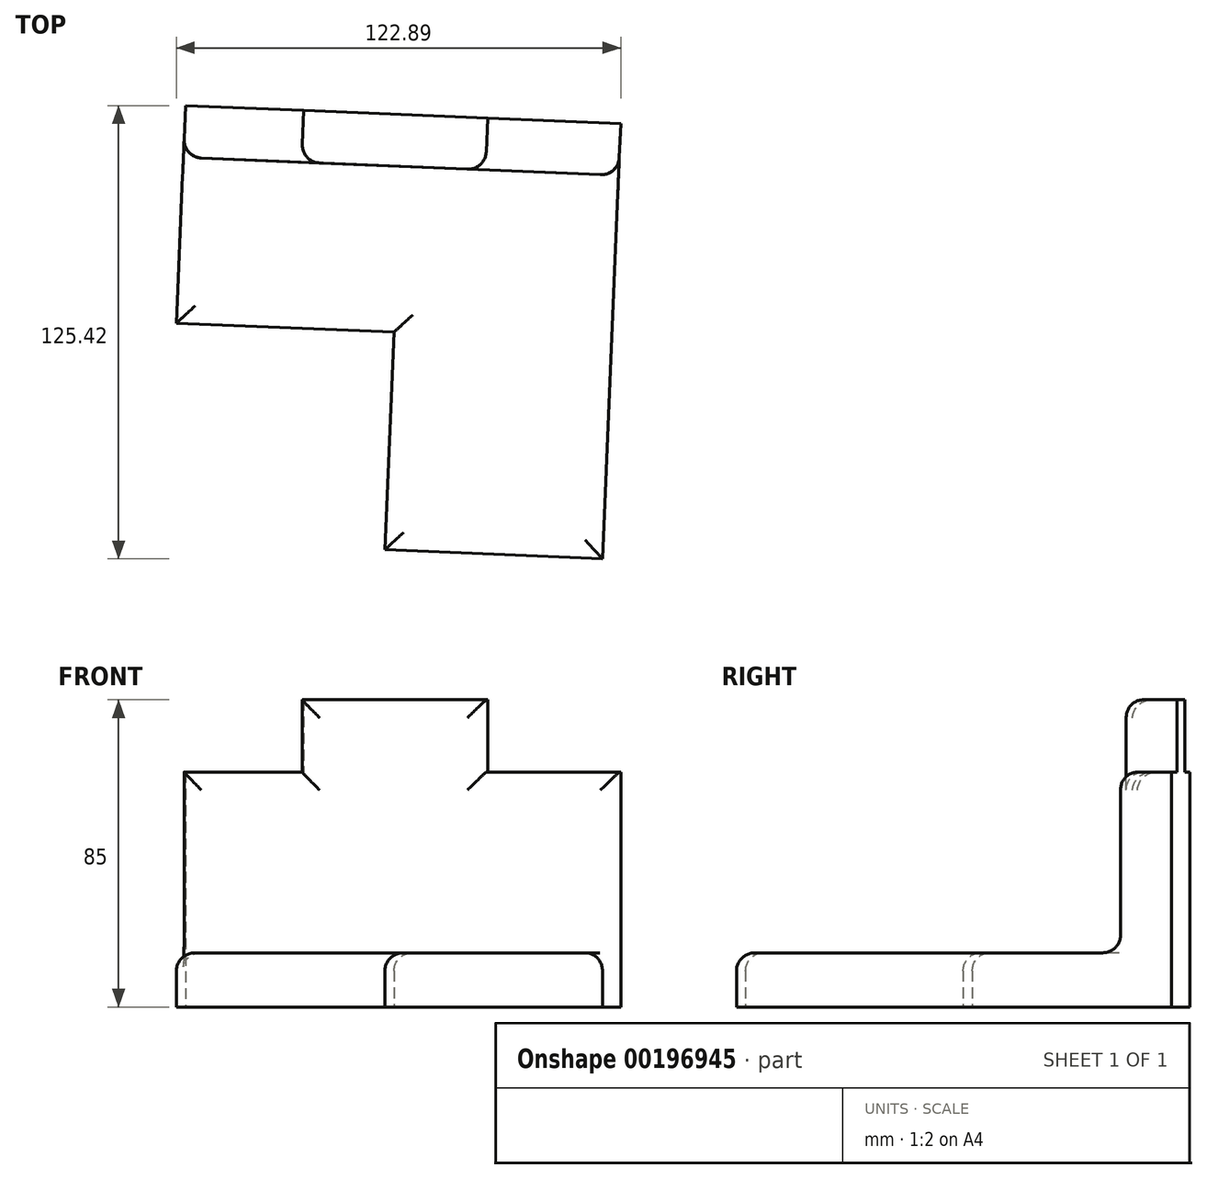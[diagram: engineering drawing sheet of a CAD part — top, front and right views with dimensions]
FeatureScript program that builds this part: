
annotation { "Feature Type Name" : "Feature", "Feature Type Description" : "" }
export const myFeature = defineFeature(function(context is Context, id is Id, definition is map)
    precondition{}
    {
        {
            var Q0;
            Q0=qCreatedBy(makeId("Top.planeOp"),FACE);
            var sketch = newSketch(context, id + "F0", { "sketchPlane" : qUnion([Q0])});
            skLineSegment(sketch, "E0.bottom", {"start": v(-60.23, 60.23) * mm, "end": v(60.23, 60.23) * mm});
            skLineSegment(sketch, "E0.top", {"start": v(0, -60.23) * mm, "end": v(60.23, -60.23) * mm});
            skLineSegment(sketch, "E0.left", {"start": v(-60.23, 60.23) * mm, "end": v(-60.23, 0) * mm});
            skLineSegment(sketch, "E0.right", {"start": v(60.23, 60.23) * mm, "end": v(60.23, -60.23) * mm});
            skPoint(sketch, "E0.middle", {"position": v(0, 0) * mm});
            skLineSegment(sketch, "E1.top", {"start": v(-60.23, 0) * mm, "end": v(0, 0) * mm});
            skLineSegment(sketch, "E1.right", {"start": v(0, -60.23) * mm, "end": v(0, 0) * mm});
            skPoint(sketch, "E2.orphan", {"position": v(-60.23, -60.23) * mm});
            skLineSegment(sketch, "E3", {"start": v(-60.23, 45.92) * mm, "end": v(60.23, 45.92) * mm});
            skSolve(sketch);
        }
        {
            var Q0;
            {var subQ2=sQuery(id+"F0.wireOp",EDGE,"E0.top");Q0=makeQuery(id+"F0.imprint","IMPRINT",FACE,{"disambiguationData":[TD([[makeQuery(id+"F0.imprint","IMPRINT",EDGE,{"derivedFrom":subQ2}),1.0]])]});}
            extrude(context, id + "F1", {"entities" : qUnion([Q0]), "depth" : 15 * mm});
        }
        {
            var Q0;
            {var subQ0=sQuery(id+"F0.wireOp",EDGE,"E0.bottom");Q0=makeQuery(id+"F0.imprint","IMPRINT",FACE,{"disambiguationData":[TD([[makeQuery(id+"F0.imprint","IMPRINT",EDGE,{"derivedFrom":subQ0}),-1.0]])]});}
            extrude(context, id + "F2", {"entities" : qUnion([Q0]), "operationType" : NewBodyOperationType.ADD, "depth" : 65 * mm});
        }
        {
            var Q0;
            Q0=makeQuery(id+"F2.opExtrude","CAP_FACE",FACE,{"disambiguationData":[OSD([sQuery(id+"F0.wireOp",EDGE,"E0.bottom"),sQuery(id+"F0.wireOp",EDGE,"E0.left"),sQuery(id+"F0.wireOp",EDGE,"E0.right"),sQuery(id+"F0.wireOp",EDGE,"E3")])],"isStart":false});
            var sketch = newSketch(context, id + "F3", { "sketchPlane" : qUnion([Q0])});
            skLineSegment(sketch, "E4", {"start": v(-27.52, 60.23) * mm, "end": v(-27.52, 45.92) * mm});
            skLineSegment(sketch, "E5", {"start": v(23.39, 60.23) * mm, "end": v(23.39, 45.92) * mm});
            skSolve(sketch);
        }
        {
            var Q0;
            {var subQ0=sQuery(id+"F3.wireOp",EDGE,"E4");Q0=makeQuery(id+"F3.imprint","IMPRINT",FACE,{"disambiguationData":[TD([[makeQuery(id+"F3.imprint","IMPRINT",EDGE,{"derivedFrom":subQ0}),1.0]])]});}
            extrude(context, id + "F4", {"entities" : qUnion([Q0]), "operationType" : NewBodyOperationType.ADD, "depth" : 20 * mm});
        }
        {
            var Q0;
            {var subQ0=sQuery(id+"F0.wireOp",EDGE,"E3");Q0=makeQuery(id+"F4.boolean.opBoolean","MERGE",FACE,{"derivedFrom":[makeQuery(id+"F2.opExtrude","SWEPT_FACE",FACE,{"disambiguationData":[OSD([subQ0])]}),makeQuery(id+"F4.opExtrude","SWEPT_FACE",FACE,{"disambiguationData":[OSD([subQ0])]})]});}
            var Q1;
            Q1=makeQuery(id+"F1.opExtrude","CAP_FACE",FACE,{"disambiguationData":[OSD([sQuery(id+"F0.wireOp",EDGE,"E0.top"),sQuery(id+"F0.wireOp",EDGE,"E0.left"),sQuery(id+"F0.wireOp",EDGE,"E0.right"),sQuery(id+"F0.wireOp",EDGE,"E1.top"),sQuery(id+"F0.wireOp",EDGE,"E1.right"),sQuery(id+"F0.wireOp",EDGE,"E3")])],"isStart":false});
            fillet(context, id + "F5", {"entities" : qUnion([Q0, Q1]), "radius" : 5 * mm, "tangentPropagation" : true, "allowEdgeOverflow" : false});
        }
        {
            var Q0;
            Q0=makeQuery(id+"F1.opExtrude","SWEPT_BODY",BODY,{"disambiguationData":[OSD([sQuery(id+"F0.wireOp",EDGE,"E0.top"),sQuery(id+"F0.wireOp",EDGE,"E0.left"),sQuery(id+"F0.wireOp",EDGE,"E0.right"),sQuery(id+"F0.wireOp",EDGE,"E1.top"),sQuery(id+"F0.wireOp",EDGE,"E1.right"),sQuery(id+"F0.wireOp",EDGE,"E3")])]});
            var Q1;
            Q1=makeQuery(id+"F2.opExtrude","SWEPT_EDGE",EDGE,{"disambiguationData":[OSD([sQuery(id+"F0.wireOp",EDGE,"E0.bottom"),sQuery(id+"F0.wireOp",EDGE,"E0.right")])]});
            transform(context, id + "F6", {"entities" : qUnion([Q0]), "transformType" : TransformType.ROTATION, "transformAxis" : qUnion([Q1]), "angle" : 2.4 * degree, "makeCopy" : false});
        }
    });
